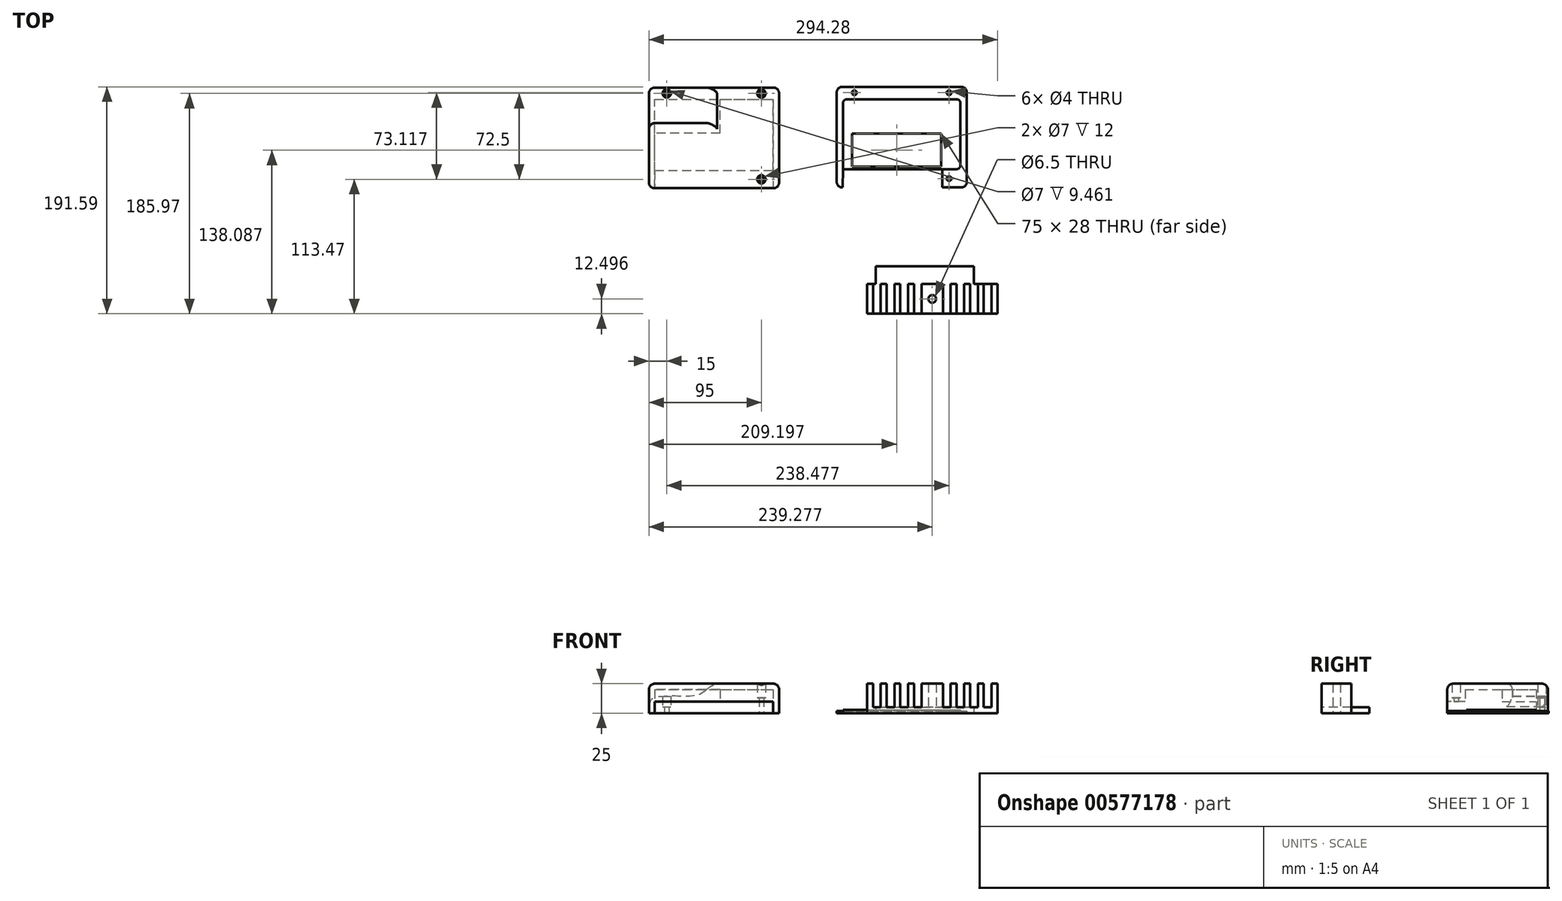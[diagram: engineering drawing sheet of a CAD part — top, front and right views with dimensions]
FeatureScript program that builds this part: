
annotation { "Feature Type Name" : "Feature", "Feature Type Description" : "" }
export const myFeature = defineFeature(function(context is Context, id is Id, definition is map)
    precondition{}
    {
        {
            var Q0;
            Q0=qCreatedBy(makeId("Top.planeOp"),FACE);
            var sketch = newSketch(context, id + "F0", { "sketchPlane" : qUnion([Q0])});
            skLineSegment(sketch, "E0.bottom", {"start": v(0, 0) * mm, "end": v(100, 0) * mm});
            skLineSegment(sketch, "E0.top", {"start": v(0, 60) * mm, "end": v(100, 60) * mm});
            skLineSegment(sketch, "E0.left", {"start": v(0, 0) * mm, "end": v(0, 60) * mm});
            skLineSegment(sketch, "E0.right", {"start": v(100, 0) * mm, "end": v(100, 60) * mm});
            skLineSegment(sketch, "E1.bottom", {"start": v(3.11, 2) * mm, "end": v(78.11, 2) * mm});
            skLineSegment(sketch, "E1.top", {"start": v(3.11, 9.5) * mm, "end": v(78.11, 9.5) * mm});
            skLineSegment(sketch, "E1.left", {"start": v(3.11, 2) * mm, "end": v(3.11, 9.5) * mm});
            skLineSegment(sketch, "E1.right", {"start": v(78.11, 2) * mm, "end": v(78.11, 9.5) * mm});
            skLineSegment(sketch, "E2.bottom", {"start": v(3.11, 30) * mm, "end": v(78.11, 30) * mm});
            skLineSegment(sketch, "E2.top", {"start": v(3.11, 22.5) * mm, "end": v(78.11, 22.5) * mm});
            skLineSegment(sketch, "E2.left", {"start": v(3.11, 30) * mm, "end": v(3.11, 22.5) * mm});
            skLineSegment(sketch, "E2.right", {"start": v(78.11, 30) * mm, "end": v(78.11, 22.5) * mm});
            skPoint(sketch, "E3", {"position": v(23.44, 17.8) * mm});
            skPoint(sketch, "E4", {"position": v(69.8, 17.8) * mm});
            skLineSegment(sketch, "E5.bottom", {"start": v(0, 70) * mm, "end": v(100, 70) * mm});
            skLineSegment(sketch, "E5.top", {"start": v(0, -15) * mm, "end": v(100, -15) * mm});
            skLineSegment(sketch, "E5.left", {"start": v(-5, 65) * mm, "end": v(-5, -10) * mm});
            skLineSegment(sketch, "E5.right", {"start": v(105, 65) * mm, "end": v(105, -10) * mm});
            skPoint(sketch, "E6.visualSharp", {"position": v(-5, 70) * mm});
            skArc(sketch, "E6.filletArc", {"start": v(0, 70) * mm, "mid": v(-3.54, 68.54) * mm, "end": v(-5, 65) * mm});
            skPoint(sketch, "E7.visualSharp", {"position": v(-5, -15) * mm});
            skArc(sketch, "E7.filletArc", {"start": v(-5, -10) * mm, "mid": v(-3.54, -13.54) * mm, "end": v(0, -15) * mm});
            skPoint(sketch, "E8.visualSharp", {"position": v(105, -15) * mm});
            skArc(sketch, "E8.filletArc", {"start": v(100, -15) * mm, "mid": v(103.54, -13.54) * mm, "end": v(105, -10) * mm});
            skPoint(sketch, "E9.visualSharp", {"position": v(105, 70) * mm});
            skArc(sketch, "E9.filletArc", {"start": v(105, 65) * mm, "mid": v(103.54, 68.54) * mm, "end": v(100, 70) * mm});
            skLineSegment(sketch, "E10", {"start": v(-13.56, 64.8) * mm, "end": v(-13.56, 34.8) * mm});
            skLineSegment(sketch, "E11", {"start": v(100, 31.37) * mm, "end": v(50, 31.37) * mm});
            skLineSegment(sketch, "E12", {"start": v(50, 31.37) * mm, "end": v(0, 31.37) * mm});
            skLineSegment(sketch, "E13", {"start": v(55, 31.37) * mm, "end": v(55, 60) * mm});
            skLineSegment(sketch, "E14", {"start": v(0, 0) * mm, "end": v(0, -15) * mm});
            skCircle(sketch, "E15", {"center": v(90, -7.5) * mm, "radius": 2 * mm});
            skCircle(sketch, "E16", {"center": v(90, 65) * mm, "radius": 2 * mm});
            skCircle(sketch, "E17", {"center": v(10, 65) * mm, "radius": 2 * mm});
            skCircle(sketch, "E18", {"center": v(10, 65) * mm, "radius": 3.5 * mm});
            skCircle(sketch, "E19", {"center": v(90, 65) * mm, "radius": 3.5 * mm});
            skCircle(sketch, "E20", {"center": v(90, -7.5) * mm, "radius": 3.5 * mm});
            skLineSegment(sketch, "E21", {"start": v(100, 0) * mm, "end": v(100, -15) * mm});
            skSolve(sketch);
        }
        {
            var Q0;
            Q0 = qSketchRegion(id + "F0", true);
            var Q1;
            Q1=makeQuery(id+"F0.imprint","IMPRINT",FACE,{"disambiguationData":[TD([[makeQuery(id+"F0.imprint","IMPRINT",EDGE,{"derivedFrom":sQuery(id+"F0.wireOp",EDGE,"E0.bottom")}),1.0]])]});
            var Q2;
            Q2=makeQuery(id+"F0.imprint","IMPRINT",FACE,{"disambiguationData":[TD([[makeQuery(id+"F0.imprint","IMPRINT",EDGE,{"derivedFrom":sQuery(id+"F0.wireOp",EDGE,"E2.bottom")}),-1.0]])]});
            var Q3;
            Q3=makeQuery(id+"F0.imprint","IMPRINT",FACE,{"disambiguationData":[TD([[makeQuery(id+"F0.imprint","IMPRINT",EDGE,{"derivedFrom":sQuery(id+"F0.wireOp",EDGE,"E1.bottom")}),1.0]])]});
            var Q4;
            {var subQ0=sQuery(id+"F0.wireOp",EDGE,"gcSXXUce-kbYd-lFcz-0eDG-yClu4jfiBCWm");Q4=makeQuery(id+"F0.imprint","IMPRINT",FACE,{"disambiguationData":[TD([[makeQuery(id+"F0.imprint","IMPRINT",EDGE,{"derivedFrom":subQ0}),-1.0]])]});}
            var Q5;
            {var subQ0=sQuery(id+"F0.wireOp",EDGE,"E12");Q5=makeQuery(id+"F0.imprint","IMPRINT",FACE,{"disambiguationData":[TD([[makeQuery(id+"F0.imprint","IMPRINT",EDGE,{"derivedFrom":subQ0}),-1.0]])]});}
            var Q6;
            {var subQ3=sQuery(id+"F0.wireOp",EDGE,"E13");Q6=makeQuery(id+"F0.imprint","IMPRINT",FACE,{"disambiguationData":[TD([[makeQuery(id+"F0.imprint","IMPRINT",EDGE,{"derivedFrom":subQ3}),-1.0]])]});}
            var Q7;
            Q7=makeQuery(id+"F0.imprint","IMPRINT",FACE,{"disambiguationData":[TD([[makeQuery(id+"F0.imprint","IMPRINT",EDGE,{"derivedFrom":sQuery(id+"F0.wireOp",EDGE,"E15")}),-1.0]])]});
            var Q8;
            Q8=makeQuery(id+"F0.imprint","IMPRINT",FACE,{"disambiguationData":[TD([[makeQuery(id+"F0.imprint","IMPRINT",EDGE,{"derivedFrom":sQuery(id+"F0.wireOp",EDGE,"E16")}),-1.0]])]});
            var Q9;
            Q9=makeQuery(id+"F0.imprint","IMPRINT",FACE,{"disambiguationData":[TD([[makeQuery(id+"F0.imprint","IMPRINT",EDGE,{"derivedFrom":sQuery(id+"F0.wireOp",EDGE,"E17")}),-1.0]])]});
            extrude(context, id + "F1", {"entities" : qUnion([Q0, Q1, Q2, Q3, Q4, Q5, Q6, Q7, Q8, Q9]), "depth" : 25 * mm, "offsetDistance" : 25 * mm});
        }
        {
            var Q0;
            Q0=makeQuery(id+"F1.opExtrude","CAP_EDGE",EDGE,{"disambiguationData":[OSD([sQuery(id+"F0.wireOp",EDGE,"E5.bottom")])],"isStart":false});
            var Q1;
            Q1=makeQuery(id+"F1.opExtrude","CAP_EDGE",EDGE,{"disambiguationData":[OSD([sQuery(id+"F0.wireOp",EDGE,"E5.left")])],"isStart":false});
            var Q2;
            Q2=makeQuery(id+"F1.opExtrude","CAP_EDGE",EDGE,{"disambiguationData":[OSD([sQuery(id+"F0.wireOp",EDGE,"E5.right")])],"isStart":false});
            fillet(context, id + "F2", {"entities" : qUnion([Q0, Q1, Q2]), "radius" : 5 * mm, "tangentPropagation" : true, "allowEdgeOverflow" : false});
        }
        {
            var Q0;
            Q0=makeQuery(id+"F0.imprint","IMPRINT",FACE,{"disambiguationData":[TD([[makeQuery(id+"F0.imprint","IMPRINT",EDGE,{"derivedFrom":sQuery(id+"F0.wireOp",EDGE,"E16")}),-1.0]])]});
            var Q1;
            Q1=makeQuery(id+"F0.imprint","IMPRINT",FACE,{"disambiguationData":[TD([[makeQuery(id+"F0.imprint","IMPRINT",EDGE,{"derivedFrom":sQuery(id+"F0.wireOp",EDGE,"E15")}),-1.0]])]});
            extrude(context, id + "F3", {"entities" : qUnion([Q0, Q1]), "operationType" : NewBodyOperationType.REMOVE, "depth" : 25 * mm, "offsetDistance" : 25 * mm, "hasSecondDirection" : true, "secondDirectionOppositeDirection" : false, "secondDirectionDepth" : 13 * mm});
        }
        {
            var Q0;
            Q0=qCreatedBy(makeId("Top.planeOp"),FACE);
            var sketch = newSketch(context, id + "F4", { "sketchPlane" : qUnion([Q0])});
            skLineSegment(sketch, "E22.bottom", {"start": v(158.98, 1.12) * mm, "end": v(254.98, 1.12) * mm});
            skLineSegment(sketch, "E22.top", {"start": v(161.98, 60.12) * mm, "end": v(254.98, 60.12) * mm});
            skLineSegment(sketch, "E22.left", {"start": v(158.98, 1.12) * mm, "end": v(158.98, 57.12) * mm});
            skLineSegment(sketch, "E22.right", {"start": v(257.98, 4.12) * mm, "end": v(257.98, 57.12) * mm});
            skLineSegment(sketch, "E23.bottom", {"start": v(166.7, 3.12) * mm, "end": v(241.7, 3.12) * mm});
            skLineSegment(sketch, "E23.top", {"start": v(166.7, 10.62) * mm, "end": v(241.7, 10.62) * mm});
            skLineSegment(sketch, "E23.left", {"start": v(166.7, 3.12) * mm, "end": v(166.7, 10.62) * mm});
            skLineSegment(sketch, "E23.right", {"start": v(241.7, 3.12) * mm, "end": v(241.7, 10.62) * mm});
            skLineSegment(sketch, "E24.bottom", {"start": v(166.7, 31.12) * mm, "end": v(241.7, 31.12) * mm});
            skLineSegment(sketch, "E24.top", {"start": v(166.7, 23.62) * mm, "end": v(241.7, 23.62) * mm});
            skLineSegment(sketch, "E24.left", {"start": v(166.7, 31.12) * mm, "end": v(166.7, 23.62) * mm});
            skLineSegment(sketch, "E24.right", {"start": v(241.7, 31.12) * mm, "end": v(241.7, 23.62) * mm});
            skPoint(sketch, "E25", {"position": v(182.42, 18.92) * mm});
            skPoint(sketch, "E26", {"position": v(228.78, 18.92) * mm});
            skLineSegment(sketch, "E27.bottom", {"start": v(158.48, 70.62) * mm, "end": v(258.48, 70.62) * mm});
            skLineSegment(sketch, "E27.top", {"start": v(158.48, -14.38) * mm, "end": v(258.48, -14.38) * mm});
            skLineSegment(sketch, "E27.left", {"start": v(153.48, 65.62) * mm, "end": v(153.48, -9.38) * mm});
            skLineSegment(sketch, "E27.right", {"start": v(263.48, 65.62) * mm, "end": v(263.48, -9.38) * mm});
            skPoint(sketch, "E28.visualSharp", {"position": v(153.48, 70.62) * mm});
            skArc(sketch, "E28.filletArc", {"start": v(158.48, 70.62) * mm, "mid": v(154.94, 69.15) * mm, "end": v(153.48, 65.62) * mm});
            skPoint(sketch, "E29.visualSharp", {"position": v(153.48, -14.38) * mm});
            skArc(sketch, "E29.filletArc", {"start": v(153.48, -9.38) * mm, "mid": v(154.94, -12.92) * mm, "end": v(158.48, -14.38) * mm});
            skPoint(sketch, "E30.visualSharp", {"position": v(263.48, -14.38) * mm});
            skArc(sketch, "E30.filletArc", {"start": v(258.48, -14.38) * mm, "mid": v(262.01, -12.92) * mm, "end": v(263.48, -9.38) * mm});
            skPoint(sketch, "E31.visualSharp", {"position": v(263.48, 70.62) * mm});
            skArc(sketch, "E31.filletArc", {"start": v(263.48, 65.62) * mm, "mid": v(262.01, 69.15) * mm, "end": v(258.48, 70.62) * mm});
            skLineSegment(sketch, "E32", {"start": v(254.8, -14.38) * mm, "end": v(254.8, 1.12) * mm});
            skLineSegment(sketch, "E33", {"start": v(158.98, 1.12) * mm, "end": v(158.48, -14.38) * mm});
            skCircle(sketch, "E34", {"center": v(182.42, 18.92) * mm, "radius": 2 * mm});
            skCircle(sketch, "E35", {"center": v(228.78, 18.92) * mm, "radius": 2 * mm});
            skLineSegment(sketch, "E36", {"start": v(166.7, 10.62) * mm, "end": v(166.7, 23.62) * mm});
            skLineSegment(sketch, "E37", {"start": v(241.7, 10.62) * mm, "end": v(241.7, 23.62) * mm});
            skLineSegment(sketch, "E38", {"start": v(242.83, 1.12) * mm, "end": v(242.83, -14.38) * mm});
            skCircle(sketch, "E39", {"center": v(248.48, 65.62) * mm, "radius": 2 * mm});
            skCircle(sketch, "E40", {"center": v(168.48, 65.62) * mm, "radius": 2 * mm});
            skCircle(sketch, "E41", {"center": v(248.48, -6.88) * mm, "radius": 2 * mm});
            skPoint(sketch, "E42.visualSharp", {"position": v(158.98, 60.12) * mm});
            skArc(sketch, "E42.filletArc", {"start": v(161.98, 60.12) * mm, "mid": v(159.86, 59.24) * mm, "end": v(158.98, 57.12) * mm});
            skPoint(sketch, "E43.visualSharp", {"position": v(257.98, 60.12) * mm});
            skArc(sketch, "E43.filletArc", {"start": v(257.98, 57.12) * mm, "mid": v(257.1, 59.24) * mm, "end": v(254.98, 60.12) * mm});
            skPoint(sketch, "E44.visualSharp", {"position": v(257.98, 1.12) * mm});
            skArc(sketch, "E44.filletArc", {"start": v(254.98, 1.12) * mm, "mid": v(257.1, 2) * mm, "end": v(257.98, 4.12) * mm});
            skSolve(sketch);
        }
        {
            var Q0;
            Q0=makeQuery(id+"F4.imprint","IMPRINT",FACE,{"disambiguationData":[TD([[makeQuery(id+"F4.imprint","IMPRINT",EDGE,{"derivedFrom":sQuery(id+"F4.wireOp",EDGE,"E22.top")}),1.0]])]});
            var Q1;
            Q1=makeQuery(id+"F4.imprint","IMPRINT",FACE,{"disambiguationData":[TD([[makeQuery(id+"F4.imprint","IMPRINT",EDGE,{"derivedFrom":sQuery(id+"F4.wireOp",EDGE,"E22.top")}),-1.0]])]});
            var Q2;
            {var subQ0=sQuery(id+"F4.wireOp",EDGE,"E32");Q2=makeQuery(id+"F4.imprint","IMPRINT",FACE,{"disambiguationData":[TD([[makeQuery(id+"F4.imprint","IMPRINT",EDGE,{"derivedFrom":subQ0}),1.0]])]});}
            extrude(context, id + "F5", {"entities" : qUnion([Q0, Q1, Q2]), "depth" : 2 * mm, "offsetDistance" : 25 * mm});
        }
        {
            var Q0;
            Q0=makeQuery(id+"F4.imprint","IMPRINT",FACE,{"disambiguationData":[TD([[makeQuery(id+"F4.imprint","IMPRINT",EDGE,{"derivedFrom":sQuery(id+"F4.wireOp",EDGE,"E22.bottom")}),1.0]])]});
            extrude(context, id + "F6", {"entities" : qUnion([Q0]), "operationType" : NewBodyOperationType.ADD, "depth" : 3 * mm, "offsetDistance" : 25 * mm});
        }
        {
            var Q0;
            Q0=makeQuery(id+"F1.opExtrude","SWEPT_FACE",FACE,{"disambiguationData":[OSD([sQuery(id+"F0.wireOp",EDGE,"E5.bottom")])]});
            var sketch = newSketch(context, id + "F7", { "sketchPlane" : qUnion([Q0])});
            skLineSegment(sketch, "E45", {"start": v(-81.24, 10) * mm, "end": v(-12.78, 10) * mm});
            skFitSpline(sketch, "E46", {"points": [v(-64.89, 23.6) * mm, v(-56.42, 25.38) * mm, v(-46.15, 22) * mm, v(-36.74, 15.61) * mm, v(-16.74, 14.5) * mm, v(-4.94, 14.05) * mm, v(2.89, 11.61) * mm, v(6.58, 1.32) * mm], "startDerivative": vector(58.62, -1.9) * mm, "endDerivative": vector(30.84, -36.08) * mm});
            skLineSegment(sketch, "E47", {"start": v(-56.42, 25.38) * mm, "end": v(5.8, 25.38) * mm});
            skLineSegment(sketch, "E48", {"start": v(5.8, 25.38) * mm, "end": v(6.58, 1.32) * mm});
            skLineSegment(sketch, "E49", {"start": v(-12.78, 10) * mm, "end": v(0, 10) * mm});
            skSolve(sketch);
        }
        {
            var Q0;
            {var subQ0=sQuery(id+"F7.wireOp",EDGE,"E46");var subQ1=sQuery(id+"F0.wireOp",EDGE,"E5.bottom");var subQ2=makeQuery(id+"F2.opFillet","BLEND_EDGE",EDGE,{"blendedFrom":[makeQuery(id+"F1.opExtrude","CAP_EDGE",EDGE,{"disambiguationData":[OSD([subQ1])],"isStart":false}),makeQuery(id+"F1.opExtrude","SWEPT_FACE",FACE,{"disambiguationData":[OSD([subQ1])]})],"blendedInto":[makeQuery(id+"F1.opExtrude","SWEPT_FACE",FACE,{"disambiguationData":[OSD([subQ1])]})]});var subQ3=makeQuery(id+"F7.imprint","INTERSECT",VERTEX,{"derivedFrom":[subQ2,subQ0]});Q0=makeQuery(id+"F7.imprint","IMPRINT",FACE,{"disambiguationData":[TD([[makeQuery(id+"F7.imprint","IMPRINT",EDGE,{"disambiguationData":[TD([[subQ3,-1.0]])],"derivedFrom":subQ0}),1.0]])]});}
            var Q1;
            {var subQ1=sQuery(id+"F7.wireOp",EDGE,"E47");Q1=makeQuery(id+"F7.imprint","IMPRINT",FACE,{"disambiguationData":[TD([[makeQuery(id+"F7.imprint","IMPRINT",EDGE,{"derivedFrom":subQ1}),-1.0]])]});}
            extrude(context, id + "F8", {"entities" : qUnion([Q0, Q1]), "operationType" : NewBodyOperationType.REMOVE, "oppositeDirection" : true, "depth" : 30 * mm, "offsetDistance" : 25 * mm});
        }
        {
            var Q0;
            Q0=makeQuery(id+"F8.boolean.opBoolean","INTERSECT",EDGE,{"derivedFrom":[makeQuery(id+"F1.opExtrude","CAP_FACE",FACE,{"disambiguationData":[OSD([sQuery(id+"F0.wireOp",EDGE,"E0.top"),sQuery(id+"F0.wireOp",EDGE,"E0.right"),sQuery(id+"F0.wireOp",EDGE,"E5.bottom"),sQuery(id+"F0.wireOp",EDGE,"E5.top"),sQuery(id+"F0.wireOp",EDGE,"E5.left"),sQuery(id+"F0.wireOp",EDGE,"E5.right"),sQuery(id+"F0.wireOp",EDGE,"E6.filletArc"),sQuery(id+"F0.wireOp",EDGE,"E7.filletArc"),sQuery(id+"F0.wireOp",EDGE,"E8.filletArc"),sQuery(id+"F0.wireOp",EDGE,"E9.filletArc"),sQuery(id+"F0.wireOp",EDGE,"gcSXXUce-kbYd-lFcz-0eDG-yClu4jfiBCWm")])],"isStart":false}),makeQuery(id+"F8.opExtrude","CAP_FACE",FACE,{"disambiguationData":[OSD([sQuery(id+"F7.wireOp",EDGE,"E46"),sQuery(id+"F7.wireOp",EDGE,"E47"),sQuery(id+"F7.wireOp",EDGE,"E48")])],"isStart":false})]});
            fillet(context, id + "F9", {"entities" : qUnion([Q0]), "radius" : 5 * mm, "tangentPropagation" : true, "allowEdgeOverflow" : false});
        }
        {
            var Q0;
            {var subQ0=sQuery(id+"F0.wireOp",EDGE,"E12");Q0=makeQuery(id+"F0.imprint","IMPRINT",FACE,{"disambiguationData":[TD([[makeQuery(id+"F0.imprint","IMPRINT",EDGE,{"derivedFrom":subQ0}),-1.0]])]});}
            var Q1;
            Q1=makeQuery(id+"F0.imprint","IMPRINT",FACE,{"disambiguationData":[TD([[makeQuery(id+"F0.imprint","IMPRINT",EDGE,{"derivedFrom":sQuery(id+"F0.wireOp",EDGE,"E0.bottom")}),-1.0]])]});
            var Q2;
            Q2=makeQuery(id+"F0.imprint","IMPRINT",FACE,{"disambiguationData":[TD([[makeQuery(id+"F0.imprint","IMPRINT",EDGE,{"derivedFrom":sQuery(id+"F0.wireOp",EDGE,"E15")}),-1.0]])]});
            extrude(context, id + "F10", {"entities" : qUnion([Q0, Q1, Q2]), "operationType" : NewBodyOperationType.REMOVE, "depth" : 10 * mm, "offsetDistance" : 25 * mm});
        }
        {
            var Q0;
            {var subQ0=sQuery(id+"F0.wireOp",EDGE,"gcSXXUce-kbYd-lFcz-0eDG-yClu4jfiBCWm");Q0=makeQuery(id+"F0.imprint","IMPRINT",FACE,{"disambiguationData":[TD([[makeQuery(id+"F0.imprint","IMPRINT",EDGE,{"derivedFrom":subQ0}),-1.0]])]});}
            var Q1;
            {var subQ0=sQuery(id+"F0.wireOp",EDGE,"E0.bottom");Q1=makeQuery(id+"F0.imprint","IMPRINT",FACE,{"disambiguationData":[TD([[makeQuery(id+"F0.imprint","IMPRINT",EDGE,{"derivedFrom":subQ0}),1.0]])]});}
            var Q2;
            Q2=makeQuery(id+"F0.imprint","IMPRINT",FACE,{"disambiguationData":[TD([[makeQuery(id+"F0.imprint","IMPRINT",EDGE,{"derivedFrom":sQuery(id+"F0.wireOp",EDGE,"E2.bottom")}),-1.0]])]});
            var Q3;
            Q3=makeQuery(id+"F0.imprint","IMPRINT",FACE,{"disambiguationData":[TD([[makeQuery(id+"F0.imprint","IMPRINT",EDGE,{"derivedFrom":sQuery(id+"F0.wireOp",EDGE,"E1.bottom")}),1.0]])]});
            var Q4;
            {var subQ3=sQuery(id+"F0.wireOp",EDGE,"E13");Q4=makeQuery(id+"F0.imprint","IMPRINT",FACE,{"disambiguationData":[TD([[makeQuery(id+"F0.imprint","IMPRINT",EDGE,{"derivedFrom":subQ3}),-1.0]])]});}
            extrude(context, id + "F11", {"entities" : qUnion([Q0, Q1, Q2, Q3, Q4]), "operationType" : NewBodyOperationType.REMOVE, "depth" : 20 * mm, "offsetDistance" : 25 * mm});
        }
        {
            var Q0;
            Q0=qCreatedBy(makeId("Top.planeOp"),FACE);
            var sketch = newSketch(context, id + "F12", { "sketchPlane" : qUnion([Q0])});
            skLineSegment(sketch, "E50", {"start": v(269.53, -95.97) * mm, "end": v(269.53, -80.97) * mm});
            skLineSegment(sketch, "E51", {"start": v(186.53, -80.97) * mm, "end": v(186.53, -95.97) * mm});
            skLineSegment(sketch, "E52", {"start": v(269.53, -95.97) * mm, "end": v(186.53, -95.97) * mm});
            skLineSegment(sketch, "E53", {"start": v(269.53, -80.97) * mm, "end": v(186.53, -80.97) * mm});
            skLineSegment(sketch, "E54.bottom", {"start": v(179.28, -95.97) * mm, "end": v(289.28, -95.97) * mm});
            skLineSegment(sketch, "E54.top", {"start": v(179.28, -120.97) * mm, "end": v(289.28, -120.97) * mm});
            skLineSegment(sketch, "E54.left", {"start": v(179.28, -95.97) * mm, "end": v(179.28, -120.97) * mm});
            skLineSegment(sketch, "E54.right", {"start": v(289.28, -95.97) * mm, "end": v(289.28, -120.97) * mm});
            skLineSegment(sketch, "E55", {"start": v(234.28, -120.97) * mm, "end": v(234.28, -95.97) * mm});
            skLineSegment(sketch, "E56", {"start": v(213.78, -120.97) * mm, "end": v(213.78, -95.97) * mm});
            skLineSegment(sketch, "E57", {"start": v(218.78, -120.97) * mm, "end": v(218.78, -95.97) * mm});
            skLineSegment(sketch, "E58", {"start": v(225.28, -120.97) * mm, "end": v(225.28, -95.97) * mm});
            skLineSegment(sketch, "E59", {"start": v(230.28, -120.97) * mm, "end": v(230.28, -95.97) * mm});
            skLineSegment(sketch, "E60", {"start": v(184.28, -120.97) * mm, "end": v(184.28, -95.97) * mm});
            skLineSegment(sketch, "E61", {"start": v(207.28, -120.97) * mm, "end": v(207.28, -95.97) * mm});
            skLineSegment(sketch, "E62", {"start": v(202.28, -120.97) * mm, "end": v(202.28, -95.97) * mm});
            skLineSegment(sketch, "E63", {"start": v(195.78, -120.97) * mm, "end": v(195.78, -95.97) * mm});
            skLineSegment(sketch, "E64", {"start": v(190.78, -120.97) * mm, "end": v(190.78, -95.97) * mm});
            skLineSegment(sketch, "E65.MirrorCS", {"start": v(238.28, -120.97) * mm, "end": v(238.28, -95.97) * mm});
            skLineSegment(sketch, "E66.MirrorCS", {"start": v(243.28, -120.97) * mm, "end": v(243.28, -95.97) * mm});
            skLineSegment(sketch, "E67.MirrorCS", {"start": v(249.78, -120.97) * mm, "end": v(249.78, -95.97) * mm});
            skLineSegment(sketch, "E68.MirrorCS", {"start": v(254.78, -120.97) * mm, "end": v(254.78, -95.97) * mm});
            skLineSegment(sketch, "E69.MirrorCS", {"start": v(261.28, -120.97) * mm, "end": v(261.28, -95.97) * mm});
            skLineSegment(sketch, "E70.MirrorCS", {"start": v(266.28, -120.97) * mm, "end": v(266.28, -95.97) * mm});
            skLineSegment(sketch, "E71.MirrorCS", {"start": v(272.78, -120.97) * mm, "end": v(272.78, -95.97) * mm});
            skLineSegment(sketch, "E72.MirrorCS", {"start": v(277.78, -120.97) * mm, "end": v(277.78, -95.97) * mm});
            skLineSegment(sketch, "E73.MirrorCS", {"start": v(284.28, -120.97) * mm, "end": v(284.28, -95.97) * mm});
            skCircle(sketch, "E74", {"center": v(234.28, -108.47) * mm, "radius": 3.25 * mm});
            skSolve(sketch);
        }
        {
            var Q0;
            Q0 = qSketchRegion(id + "F12", true);
            extrude(context, id + "F13", {"entities" : qUnion([Q0]), "depth" : 5 * mm, "offsetDistance" : 25 * mm});
        }
        {
            var Q0;
            {var subQ0=sQuery(id+"F12.wireOp",EDGE,"E54.left");Q0=makeQuery(id+"F12.imprint","IMPRINT",FACE,{"disambiguationData":[TD([[makeQuery(id+"F12.imprint","IMPRINT",EDGE,{"derivedFrom":subQ0}),1.0]])]});}
            var Q1;
            {var subQ0=sQuery(id+"F12.wireOp",EDGE,"E63");Q1=makeQuery(id+"F12.imprint","IMPRINT",FACE,{"disambiguationData":[TD([[makeQuery(id+"F12.imprint","IMPRINT",EDGE,{"derivedFrom":subQ0}),1.0]])]});}
            var Q2;
            {var subQ0=sQuery(id+"F12.wireOp",EDGE,"E61");Q2=makeQuery(id+"F12.imprint","IMPRINT",FACE,{"disambiguationData":[TD([[makeQuery(id+"F12.imprint","IMPRINT",EDGE,{"derivedFrom":subQ0}),1.0]])]});}
            var Q3;
            {var subQ0=sQuery(id+"F12.wireOp",EDGE,"E56");Q3=makeQuery(id+"F12.imprint","IMPRINT",FACE,{"disambiguationData":[TD([[makeQuery(id+"F12.imprint","IMPRINT",EDGE,{"derivedFrom":subQ0}),-1.0]])]});}
            var Q4;
            {var subQ0=sQuery(id+"F12.wireOp",EDGE,"E58");Q4=makeQuery(id+"F12.imprint","IMPRINT",FACE,{"disambiguationData":[TD([[makeQuery(id+"F12.imprint","IMPRINT",EDGE,{"derivedFrom":subQ0}),-1.0]])]});}
            var Q5;
            {var subQ0=sQuery(id+"F12.wireOp",EDGE,"E55");Q5=makeQuery(id+"F12.imprint","IMPRINT",FACE,{"disambiguationData":[TD([[makeQuery(id+"F12.imprint","IMPRINT",EDGE,{"derivedFrom":subQ0}),1.0]])]});}
            var Q6;
            {var subQ0=sQuery(id+"F12.wireOp",EDGE,"E55");Q6=makeQuery(id+"F12.imprint","IMPRINT",FACE,{"disambiguationData":[TD([[makeQuery(id+"F12.imprint","IMPRINT",EDGE,{"derivedFrom":subQ0}),-1.0]])]});}
            var Q7;
            {var subQ0=sQuery(id+"F12.wireOp",EDGE,"E65.MirrorCS");Q7=makeQuery(id+"F12.imprint","IMPRINT",FACE,{"disambiguationData":[TD([[makeQuery(id+"F12.imprint","IMPRINT",EDGE,{"derivedFrom":subQ0}),-1.0]])]});}
            var Q8;
            {var subQ0=sQuery(id+"F12.wireOp",EDGE,"E67.MirrorCS");Q8=makeQuery(id+"F12.imprint","IMPRINT",FACE,{"disambiguationData":[TD([[makeQuery(id+"F12.imprint","IMPRINT",EDGE,{"derivedFrom":subQ0}),-1.0]])]});}
            var Q9;
            {var subQ0=sQuery(id+"F12.wireOp",EDGE,"E69.MirrorCS");Q9=makeQuery(id+"F12.imprint","IMPRINT",FACE,{"disambiguationData":[TD([[makeQuery(id+"F12.imprint","IMPRINT",EDGE,{"derivedFrom":subQ0}),-1.0]])]});}
            var Q10;
            {var subQ0=sQuery(id+"F12.wireOp",EDGE,"E71.MirrorCS");Q10=makeQuery(id+"F12.imprint","IMPRINT",FACE,{"disambiguationData":[TD([[makeQuery(id+"F12.imprint","IMPRINT",EDGE,{"derivedFrom":subQ0}),-1.0]])]});}
            var Q11;
            {var subQ0=sQuery(id+"F12.wireOp",EDGE,"E54.right");Q11=makeQuery(id+"F12.imprint","IMPRINT",FACE,{"disambiguationData":[TD([[makeQuery(id+"F12.imprint","IMPRINT",EDGE,{"derivedFrom":subQ0}),-1.0]])]});}
            extrude(context, id + "F14", {"entities" : qUnion([Q0, Q1, Q2, Q3, Q4, Q5, Q6, Q7, Q8, Q9, Q10, Q11]), "operationType" : NewBodyOperationType.ADD, "depth" : 25 * mm, "offsetDistance" : 25 * mm});
        }
        {
            var Q0;
            Q0=makeQuery(id+"F0.imprint","IMPRINT",FACE,{"disambiguationData":[TD([[makeQuery(id+"F0.imprint","IMPRINT",EDGE,{"derivedFrom":sQuery(id+"F0.wireOp",EDGE,"E17")}),-1.0]])]});
            extrude(context, id + "F15", {"entities" : qUnion([Q0]), "operationType" : NewBodyOperationType.REMOVE, "depth" : 15 * mm, "offsetDistance" : 25 * mm, "hasSecondDirection" : true, "secondDirectionOppositeDirection" : false, "secondDirectionDepth" : 5 * mm});
        }
    });
